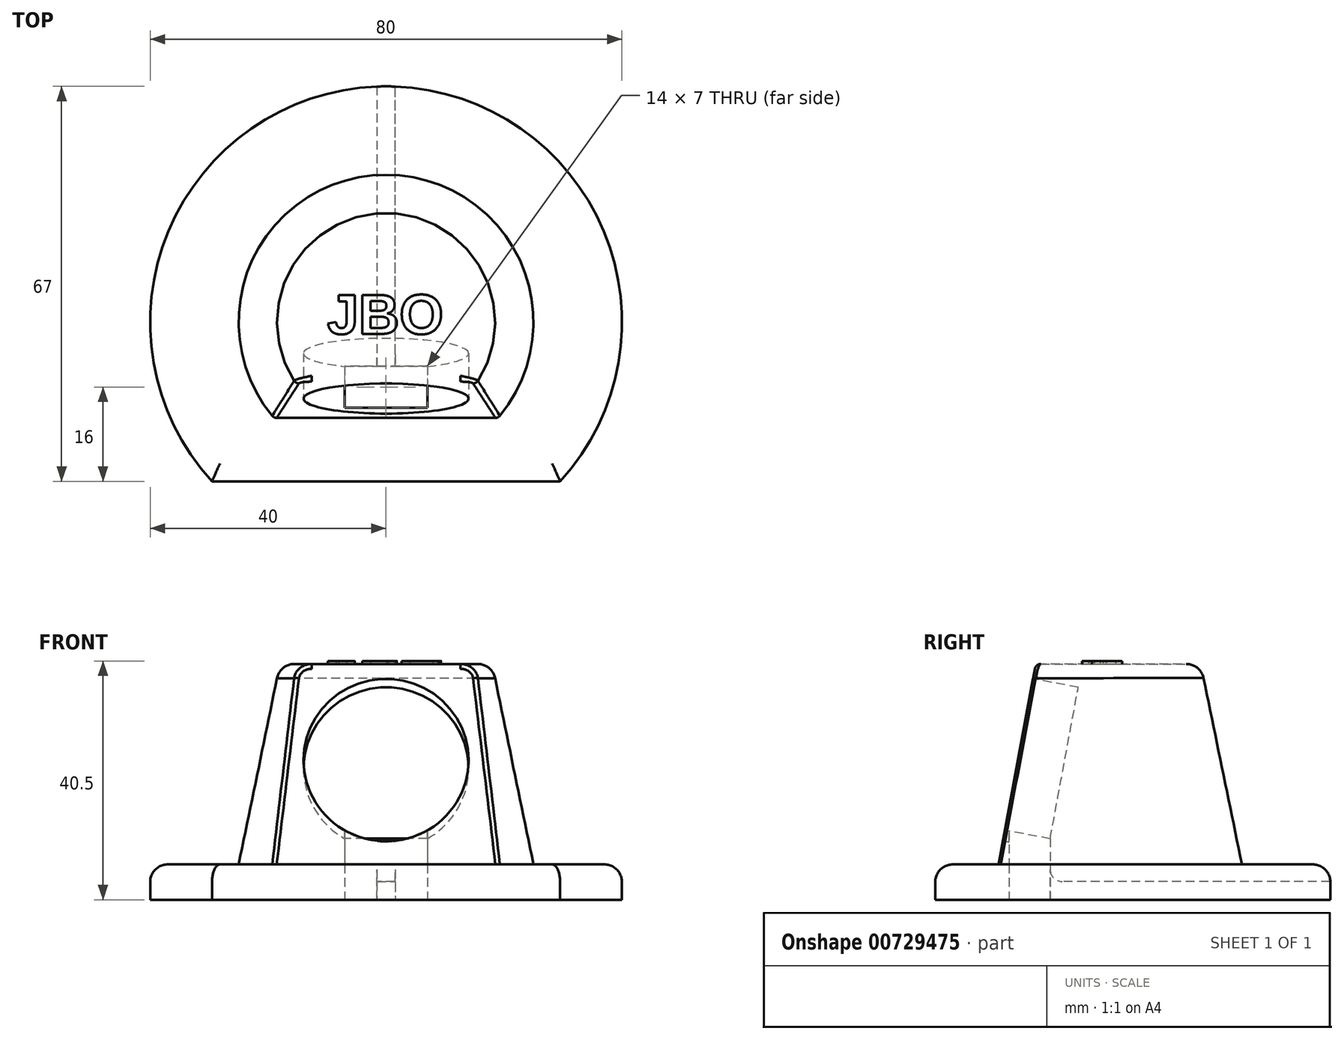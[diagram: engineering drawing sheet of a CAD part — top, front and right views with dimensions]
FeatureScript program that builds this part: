
annotation { "Feature Type Name" : "Feature", "Feature Type Description" : "" }
export const myFeature = defineFeature(function(context is Context, id is Id, definition is map)
    precondition{}
    {
        {
            var Q0;
            Q0=qCreatedBy(makeId("Top.planeOp"),FACE);
            var sketch = newSketch(context, id + "F0", { "sketchPlane" : qUnion([Q0])});
            skCircle(sketch, "E0", {"center": v(0, 0) * mm, "radius": 40 * mm});
            skLineSegment(sketch, "E1", {"start": v(-29.51, -27) * mm, "end": v(29.51, -27) * mm});
            skSolve(sketch);
        }
        {
            var Q0;
            {var subQ0=sQuery(id+"F0.wireOp",EDGE,"E1");Q0=makeQuery(id+"F0.imprint","IMPRINT",FACE,{"disambiguationData":[TD([[makeQuery(id+"F0.imprint","IMPRINT",EDGE,{"derivedFrom":subQ0}),1.0]])]});}
            extrude(context, id + "F1", {"entities" : qUnion([Q0]), "depth" : 6 * mm, "offsetDistance" : 25 * mm});
        }
        {
            var Q0;
            Q0=makeQuery(id+"F1.opExtrude","CAP_FACE",FACE,{"disambiguationData":[OSD([sQuery(id+"F0.wireOp",EDGE,"E0")])],"isStart":false});
            var sketch = newSketch(context, id + "F2", { "sketchPlane" : qUnion([Q0])});
            skCircle(sketch, "E2", {"center": v(0, 0) * mm, "radius": 25 * mm});
            skLineSegment(sketch, "E3", {"start": v(-19, -16.25) * mm, "end": v(19, -16.25) * mm});
            skSolve(sketch);
        }
        {
            var Q0;
            Q0=qCreatedBy(makeId("Top.planeOp"),FACE);
            cPlane(context, id + "F3", {"entities" : qUnion([Q0]), "cplaneType" : CPlaneType.OFFSET, "offset" : 40 * mm, "width" : 150 * mm, "height" : 150 * mm});
        }
        {
            var Q0;
            Q0=qCreatedBy(id+"F3.planeOp",FACE);
            var sketch = newSketch(context, id + "F4", { "sketchPlane" : qUnion([Q0])});
            skCircle(sketch, "E4", {"center": v(0, 0) * mm, "radius": 18 * mm});
            skLineSegment(sketch, "E5", {"start": v(-15, -9.95) * mm, "end": v(15, -9.95) * mm});
            skSolve(sketch);
        }
        {
            var Q0;
            {var subQ0=sQuery(id+"F2.wireOp",EDGE,"E3");Q0=makeQuery(id+"F2.imprint","IMPRINT",FACE,{"disambiguationData":[TD([[makeQuery(id+"F2.imprint","IMPRINT",EDGE,{"derivedFrom":subQ0}),1.0]])]});}
            var Q1;
            {var subQ0=sQuery(id+"F4.wireOp",EDGE,"E5");Q1=makeQuery(id+"F4.imprint","IMPRINT",FACE,{"disambiguationData":[TD([[makeQuery(id+"F4.imprint","IMPRINT",EDGE,{"derivedFrom":subQ0}),1.0]])]});}
            loft(context, id + "F5", {"sheetProfilesArray" : [{ "sheetProfileEntities" : qUnion([Q0]) }, { "sheetProfileEntities" : qUnion([Q1]) }]});
        }
        {
            var Q0;
            {var subQ0=sQuery(id+"F4.wireOp",EDGE,"E5");var subQ1=sQuery(id+"F4.wireOp",EDGE,"E4");var subQ2=sQuery(id+"F2.wireOp",EDGE,"E3");var subQ3=sQuery(id+"F2.wireOp",EDGE,"E2");Q0=makeQuery(id+"F5.opLoft","SWEPT_FACE",FACE,{"disambiguationData":[OSD([subQ3,subQ2,subQ1,subQ0]),TDD([makeQuery(id+"F2.imprint","INTERSECT",VERTEX,{"disambiguationData":[OD(0.0)],"derivedFrom":[subQ3,subQ2]}),makeQuery(id+"F2.imprint","INTERSECT",VERTEX,{"disambiguationData":[OD(1.0)],"derivedFrom":[subQ3,subQ2]}),makeQuery(id+"F2.imprint","IMPRINT",EDGE,{"derivedFrom":subQ2}),makeQuery(id+"F4.imprint","INTERSECT",VERTEX,{"disambiguationData":[OD(0.0)],"derivedFrom":[subQ1,subQ0]}),makeQuery(id+"F4.imprint","INTERSECT",VERTEX,{"disambiguationData":[OD(1.0)],"derivedFrom":[subQ1,subQ0]}),makeQuery(id+"F4.imprint","IMPRINT",EDGE,{"derivedFrom":subQ0})])]});}
            var sketch = newSketch(context, id + "F6", { "sketchPlane" : qUnion([Q0])});
            skCircle(sketch, "E6", {"center": v(0, 20.94) * mm, "radius": 14 * mm});
            skSolve(sketch);
        }
        {
            var Q0;
            Q0=makeQuery(id+"F1.opExtrude","CAP_FACE",FACE,{"disambiguationData":[OSD([sQuery(id+"F0.wireOp",EDGE,"E0"),sQuery(id+"F0.wireOp",EDGE,"E1")])],"isStart":true});
            var sketch = newSketch(context, id + "F7", { "sketchPlane" : qUnion([Q0])});
            skLineSegment(sketch, "E7.bottom", {"start": v(-7, 14.5) * mm, "end": v(7, 14.5) * mm});
            skLineSegment(sketch, "E7.top", {"start": v(-7, 7.5) * mm, "end": v(7, 7.5) * mm});
            skLineSegment(sketch, "E7.left", {"start": v(-7, 14.5) * mm, "end": v(-7, 7.5) * mm});
            skLineSegment(sketch, "E7.right", {"start": v(7, 14.5) * mm, "end": v(7, 7.5) * mm});
            skSolve(sketch);
        }
        {
            var Q0;
            Q0=makeQuery(id+"F1.opExtrude","CAP_FACE",FACE,{"disambiguationData":[OSD([sQuery(id+"F0.wireOp",EDGE,"E0"),sQuery(id+"F0.wireOp",EDGE,"E1")])],"isStart":true});
            var sketch = newSketch(context, id + "F8", { "sketchPlane" : qUnion([Q0])});
            skLineSegment(sketch, "E8", {"start": v(-1.55, -39.97) * mm, "end": v(-1.55, 13) * mm});
            skLineSegment(sketch, "E9", {"start": v(-1.55, 13) * mm, "end": v(1.55, 13) * mm});
            skLineSegment(sketch, "E10", {"start": v(1.55, 13) * mm, "end": v(1.55, -39.97) * mm});
            skSolve(sketch);
        }
        {
            var Q0;
            {var subQ0=sQuery(id+"F8.wireOp",EDGE,"E9");Q0=makeQuery(id+"F8.imprint","IMPRINT",FACE,{"disambiguationData":[TD([[makeQuery(id+"F8.imprint","IMPRINT",EDGE,{"derivedFrom":subQ0}),-1.0]])]});}
            var Q1;
            {var subQ0=sQuery(id+"F8.wireOp",EDGE,"E8");var subQ1=makeQuery(id+"F1.opExtrude","CAP_EDGE",EDGE,{"disambiguationData":[OSD([sQuery(id+"F0.wireOp",EDGE,"E0")])],"isStart":true});var subQ2=makeQuery(id+"F8.imprint","INTERSECT",VERTEX,{"derivedFrom":[subQ1,subQ0]});Q1=makeQuery(id+"F8.imprint","IMPRINT",FACE,{"disambiguationData":[TD([[makeQuery(id+"F8.imprint","IMPRINT",EDGE,{"disambiguationData":[TD([[subQ2,1.0]])],"derivedFrom":subQ1}),-1.0]])]});}
            extrude(context, id + "F9", {"entities" : qUnion([Q0, Q1]), "operationType" : NewBodyOperationType.REMOVE, "oppositeDirection" : true, "depth" : 3.1 * mm, "offsetDistance" : 25 * mm});
        }
        {
            var Q0;
            Q0=makeQuery(id+"F6.imprint","IMPRINT",FACE,{"disambiguationData":[TD([[makeQuery(id+"F6.imprint","IMPRINT",EDGE,{"derivedFrom":sQuery(id+"F6.wireOp",EDGE,"E6")}),1.0]])]});
            extrude(context, id + "F10", {"entities" : qUnion([Q0]), "operationType" : NewBodyOperationType.REMOVE, "oppositeDirection" : true, "depth" : 7.8 * mm, "offsetDistance" : 25 * mm});
        }
        {
            var Q0;
            Q0=makeQuery(id+"F1.opExtrude","CAP_EDGE",EDGE,{"disambiguationData":[OSD([sQuery(id+"F0.wireOp",EDGE,"E1")])],"isStart":false});
            var Q1;
            Q1=makeQuery(id+"F1.opExtrude","CAP_EDGE",EDGE,{"disambiguationData":[OSD([sQuery(id+"F0.wireOp",EDGE,"E0")])],"isStart":false});
            var Q2;
            {var subQ0=sQuery(id+"F4.wireOp",EDGE,"E5");var subQ1=sQuery(id+"F4.wireOp",EDGE,"E4");var subQ2=makeQuery(id+"F4.imprint","INTERSECT",VERTEX,{"disambiguationData":[OD(0.0)],"derivedFrom":[subQ1,subQ0]});var subQ3=makeQuery(id+"F4.imprint","INTERSECT",VERTEX,{"disambiguationData":[OD(1.0)],"derivedFrom":[subQ1,subQ0]});Q2=makeQuery(id+"F5.opLoft","MID_CAP_EDGE",EDGE,{"disambiguationData":[OSD([subQ1,subQ0]),TDD([subQ2,subQ3,makeQuery(id+"F4.imprint","IMPRINT",EDGE,{"disambiguationData":[TD([[subQ2,1.0]])],"derivedFrom":subQ1})])],"capPos":1.0});}
            fillet(context, id + "F11", {"entities" : qUnion([Q0, Q1, Q2]), "radius" : 3 * mm, "tangentPropagation" : true, "allowEdgeOverflow" : false});
        }
        {
            var Q0;
            {var subQ0=sQuery(id+"F4.wireOp",EDGE,"E5");var subQ1=sQuery(id+"F4.wireOp",EDGE,"E4");var subQ2=sQuery(id+"F2.wireOp",EDGE,"E3");var subQ3=sQuery(id+"F2.wireOp",EDGE,"E2");Q0=makeQuery(id+"F5.opLoft","SWEPT_EDGE",EDGE,{"disambiguationData":[OSD([subQ3,subQ2,subQ1,subQ0]),TDD([makeQuery(id+"F2.imprint","INTERSECT",VERTEX,{"disambiguationData":[OD(0.0)],"derivedFrom":[subQ3,subQ2]}),makeQuery(id+"F4.imprint","INTERSECT",VERTEX,{"disambiguationData":[OD(0.0)],"derivedFrom":[subQ1,subQ0]})])]});}
            fillet(context, id + "F12", {"entities" : qUnion([Q0]), "radius" : 1 * mm, "tangentPropagation" : true, "allowEdgeOverflow" : false});
        }
        {
            var Q0;
            Q0=makeQuery(id+"F7.imprint","IMPRINT",FACE,{"disambiguationData":[TD([[makeQuery(id+"F7.imprint","IMPRINT",EDGE,{"derivedFrom":sQuery(id+"F7.wireOp",EDGE,"E7.bottom")}),-1.0]])]});
            extrude(context, id + "F13", {"entities" : qUnion([Q0]), "operationType" : NewBodyOperationType.REMOVE, "oppositeDirection" : true, "depth" : 20 * mm, "offsetDistance" : 25 * mm});
        }
        {
            var Q0;
            Q0=makeQuery(id+"F13.boolean.opBoolean","INTERSECT",EDGE,{"derivedFrom":[makeQuery(id+"F9.boolean.opBoolean","COPY",FACE,{"derivedFrom":makeQuery(id+"F9.opExtrude","CAP_FACE",FACE,{"disambiguationData":[OSD([sQuery(id+"F0.wireOp",EDGE,"E0"),sQuery(id+"F8.wireOp",EDGE,"E8"),sQuery(id+"F8.wireOp",EDGE,"E9"),sQuery(id+"F8.wireOp",EDGE,"E10")])],"isStart":false})}),makeQuery(id+"F13.opExtrude","SWEPT_FACE",FACE,{"disambiguationData":[OSD([sQuery(id+"F7.wireOp",EDGE,"E7.top")])]})]});
            fillet(context, id + "F14", {"entities" : qUnion([Q0]), "radius" : 2 * mm, "tangentPropagation" : true, "allowEdgeOverflow" : false});
        }
        {
            var Q0;
            {var subQ0=sQuery(id+"F4.wireOp",EDGE,"E5");Q0=makeQuery(id+"F5.opLoft","CAP_FACE",FACE,{"disambiguationData":[OSD([makeQuery(id+"F4.imprint","IMPRINT",FACE,{"disambiguationData":[TD([[makeQuery(id+"F4.imprint","IMPRINT",EDGE,{"derivedFrom":subQ0}),1.0]])]})])],"isStart":true});}
            var sketch = newSketch(context, id + "F15", { "sketchPlane" : qUnion([Q0])});
            skText(sketch, "E11", { "text": "JBO", "fontName": "Arimo-Bold.ttf"});
            const initialGuessF15  = {"E11": [-0.01, -0.002, 1, 0, 0.00691]};
            skSetInitialGuess(sketch, initialGuessF15);
            skSolve(sketch);
        }
        {
            var Q0;
            Q0=makeQuery(id+"F15.imprint","IMPRINT",FACE,{"disambiguationData":[TD([[makeQuery(id+"F15.imprint","IMPRINT",EDGE,{"derivedFrom":sQuery(id+"F15.wireOp",EDGE,"E11.sketch_text.stroke-0")}),-1.0]])]});
            var Q1;
            Q1=makeQuery(id+"F15.imprint","IMPRINT",FACE,{"disambiguationData":[TD([[makeQuery(id+"F15.imprint","IMPRINT",EDGE,{"derivedFrom":sQuery(id+"F15.wireOp",EDGE,"E11.sketch_text.stroke-14")}),-1.0]])]});
            var Q2;
            Q2=makeQuery(id+"F15.imprint","IMPRINT",FACE,{"disambiguationData":[TD([[makeQuery(id+"F15.imprint","IMPRINT",EDGE,{"derivedFrom":sQuery(id+"F15.wireOp",EDGE,"E11.sketch_text.stroke-38")}),-1.0]])]});
            extrude(context, id + "F16", {"entities" : qUnion([Q0, Q1, Q2]), "operationType" : NewBodyOperationType.ADD, "depth" : 0.5 * mm, "offsetDistance" : 25 * mm});
        }
    });
